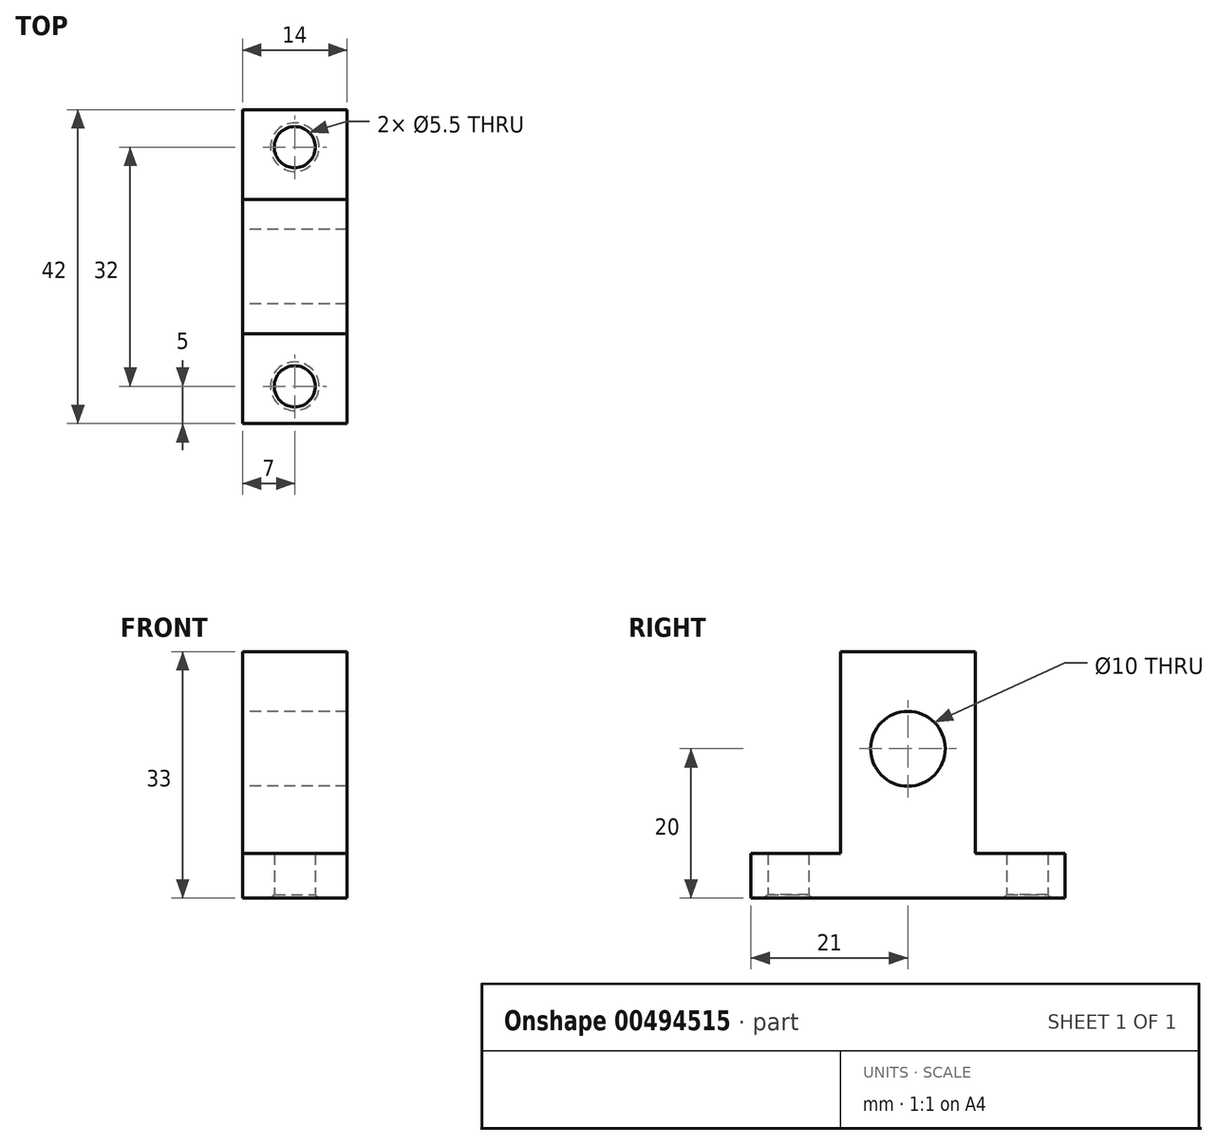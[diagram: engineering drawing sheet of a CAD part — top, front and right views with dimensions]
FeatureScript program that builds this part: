
annotation { "Feature Type Name" : "Feature", "Feature Type Description" : "" }
export const myFeature = defineFeature(function(context is Context, id is Id, definition is map)
    precondition{}
    {
        {
            var Q0;
            Q0=qCreatedBy(makeId("Right.planeOp"),FACE);
            var sketch = newSketch(context, id + "F0", { "sketchPlane" : qUnion([Q0])});
            skCircle(sketch, "E0", {"center": v(0, 0) * mm, "radius": 5 * mm});
            skLineSegment(sketch, "E1", {"start": v(0, 0) * mm, "end": v(0, -20) * mm, "construction": true});
            skLineSegment(sketch, "E2", {"start": v(0, -20) * mm, "end": v(-21, -20) * mm});
            skLineSegment(sketch, "E3", {"start": v(-21, -20) * mm, "end": v(-21, -14) * mm});
            skLineSegment(sketch, "E4", {"start": v(-21, -14) * mm, "end": v(-9, -14) * mm});
            skLineSegment(sketch, "E5", {"start": v(-9, -14) * mm, "end": v(-9, 13) * mm});
            skLineSegment(sketch, "E6", {"start": v(-9, 13) * mm, "end": v(0, 13) * mm});
            skLineSegment(sketch, "E7", {"start": v(0, 0) * mm, "end": v(0, 13) * mm, "construction": true});
            skLineSegment(sketch, "E8.MirrorCS", {"start": v(0, -20) * mm, "end": v(21, -20) * mm});
            skLineSegment(sketch, "E9.MirrorCS", {"start": v(21, -20) * mm, "end": v(21, -14) * mm});
            skLineSegment(sketch, "E10.MirrorCS", {"start": v(21, -14) * mm, "end": v(9, -14) * mm});
            skLineSegment(sketch, "E11.MirrorCS", {"start": v(9, -14) * mm, "end": v(9, 13) * mm});
            skLineSegment(sketch, "E12.MirrorCS", {"start": v(9, 13) * mm, "end": v(0, 13) * mm});
            skSolve(sketch);
        }
        {
            var Q0;
            Q0=makeQuery(id+"F0.imprint","IMPRINT",FACE,{"disambiguationData":[TD([[makeQuery(id+"F0.imprint","IMPRINT",EDGE,{"derivedFrom":sQuery(id+"F0.wireOp",EDGE,"E0")}),-1.0]])]});
            extrude(context, id + "F1", {"entities" : qUnion([Q0]), "depth" : 14 * mm, "offsetDistance" : 25 * mm});
        }
        {
            var Q0;
            Q0=makeQuery(id+"F1.opExtrude","SWEPT_FACE",FACE,{"disambiguationData":[OSD([sQuery(id+"F0.wireOp",EDGE,"E2"),sQuery(id+"F0.wireOp",EDGE,"E8.MirrorCS")])]});
            var sketch = newSketch(context, id + "F2", { "sketchPlane" : qUnion([Q0])});
            skPoint(sketch, "E13", {"position": v(7, -16) * mm});
            skPoint(sketch, "E13.positionSnap0", {"position": v(7, -21) * mm});
            skLineSegment(sketch, "E14", {"start": v(14, 0) * mm, "end": v(0, 0) * mm, "construction": true});
            skPoint(sketch, "E15.MirrorP", {"position": v(7, 16) * mm});
            skSolve(sketch);
        }
        {
            var Q0;
            Q0=sQuery(id+"F2.wireOp",VERTEX,"E13");
            var Q1;
            Q1=sQuery(id+"F2.wireOp",VERTEX,"E15.MirrorP");
            var Q2;
            Q2=makeQuery(id+"F1.opExtrude","SWEPT_BODY",BODY,{"disambiguationData":[OSD([sQuery(id+"F0.wireOp",EDGE,"E0"),sQuery(id+"F0.wireOp",EDGE,"E2"),sQuery(id+"F0.wireOp",EDGE,"E3"),sQuery(id+"F0.wireOp",EDGE,"E4"),sQuery(id+"F0.wireOp",EDGE,"E5"),sQuery(id+"F0.wireOp",EDGE,"E6"),sQuery(id+"F0.wireOp",EDGE,"E8.MirrorCS"),sQuery(id+"F0.wireOp",EDGE,"E9.MirrorCS"),sQuery(id+"F0.wireOp",EDGE,"E10.MirrorCS"),sQuery(id+"F0.wireOp",EDGE,"E11.MirrorCS"),sQuery(id+"F0.wireOp",EDGE,"E12.MirrorCS")])]});
            hole(context, id + "F3", {"style" : HoleStyle.C_SINK, "endStyle" : HoleEndStyle.THROUGH, "holeDiameter" : 5.5 * mm, "cSinkDiameter" : 6.5 * mm, "cSinkAngle" : 90 * degree, "locations" : qUnion([Q0, Q1]), "scope" : qUnion([Q2]), "isTappedThrough" : true});
        }
    });
